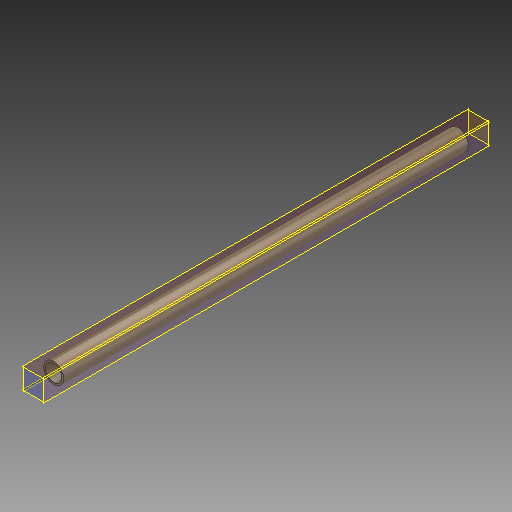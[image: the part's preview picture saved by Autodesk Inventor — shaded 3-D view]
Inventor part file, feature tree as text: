
AUTODESK INVENTOR PART (.ipt)
format: ipt  version: 2018 (Build 220112000, 112)  size: 97,792 bytes
history: native  units: mm
features: other x5, extrude x1, sketch x1
ambient origin geometry x8: Origin, YZ Plane, XZ Plane, XY Plane, X Axis, Y Axis, Z Axis, Center Point
bodies: Body1 (feature_tree)
feature tree (7):
  other  "ソリッド1"
  extrude  "押し出し1"  Depth=27.2mm
  other  "作業平面4"
  other  "作業平面5"
  other  "作業平面6"
  other  "作業平面7"
  sketch  "スケッチ1"
